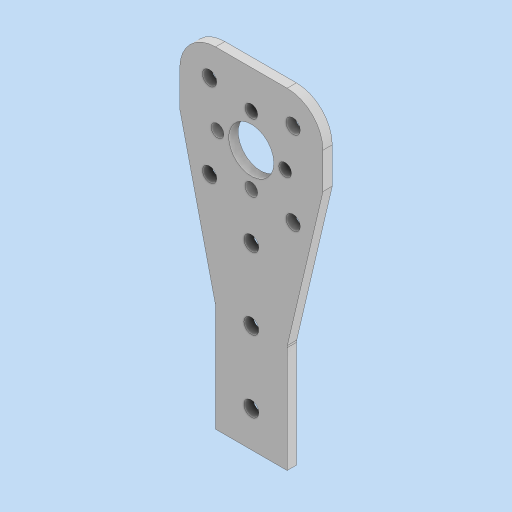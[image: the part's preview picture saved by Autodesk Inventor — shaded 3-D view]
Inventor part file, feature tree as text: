
AUTODESK INVENTOR PART (.ipt)
format: ipt  version: 2024 (Build 280153000, 153)  size: 167,936 bytes
history: native  units: in
note: dims shown in document units (in); Inventor stores cm internally (conversion verified against a paired STEP export)
features: fillet x3, extrude x1, sketch x1
ambient origin geometry x8: Origin, YZ Plane, XZ Plane, XY Plane, X Axis, Y Axis, Z Axis, Center Point
bodies: Solid1 (feature_tree)
feature tree (5):
  extrude  "Extrusion1"  Depth=0.5in
  fillet  "Fillet13"  Radius=0.209in
  fillet  "Fillet14"  Radius=0.875in
  fillet  "Fillet15"  Radius=0.13in
  sketch  "Sketch1"  dims[d2=0.6299in d3=0.209in d4=0.209in d5=0.875in d10=0.13in d11=0.0in d24=0.125in d25=0.125in d26=1.0in d27=1.5in d28=1.0in d29=1.125in d30=2.125in d31=0.177in d32=0.4724in d33=0.4724in d34=0.4724in d35=0.4724in d36=1.65in d37=0.201in d38=0.583in d39=1.5748in d41=360.0deg d43=2.0in d44=0.0in d45=1.0in d46=1.0in d47=1.0in d48=0.5in d16=0.0in d17=0.0in d18=0.0in d19=0.0in d20=0.0in d21=0.0in d22=0.0in d23=0.0in]
